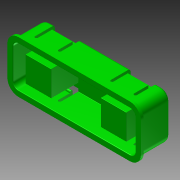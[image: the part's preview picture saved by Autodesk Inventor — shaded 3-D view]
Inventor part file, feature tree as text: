
AUTODESK INVENTOR PART (.ipt)
format: ipt  version: 2015 (Build 190159000, 159)  size: 282,624 bytes
history: native  units: in
note: dims shown in document units (in); Inventor stores cm internally (conversion verified against a paired STEP export)
features: fillet x6, extrude x4, sketch x3, shell x2, plane x2, mirror x2
ambient origin geometry x8: Origin, YZ Plane, XZ Plane, XY Plane, X Axis, Y Axis, Z Axis, Center Point
bodies: Solid1 (feature_tree)
feature tree (19):
  extrude  "Extrusion1"  Depth=0.465in
  fillet  "Fillet1"  Radius=0.57in
  shell  "Shell1"  Thickness=0.2in
  sketch  "Sketch2"  dims[d7=0.46in d8=0.2283in]
  plane  "Work Plane1"
  sketch  "Sketch3"  dims[d9=-0.033in d10=0.47in d11=0.0in d12=0.005in d13=0.01in d14=0.47in d15=0.05in d16=0.1in d17=0.05in d18=0.05in d19=0.15in d20=0.0in d21=0.125in d22=0.0in d23=0.05in d24=0.03in d26=0.445in d27=0.445in d28=0.05in]
  shell  "Shell2"  Thickness=0.1in
  extrude  "Extrusion3"  Depth=0.46in
  plane  "Work Plane2"
  extrude  "Extrusion4"  Depth=0.47in TaperAngle=0.0deg
  fillet  "Fillet6"  Radius=0.005in
  fillet  "Fillet3"  Radius=0.01in
  fillet  "Fillet4"  Radius=0.47in
  extrude  "Extrusion2"  Depth=0.05in
  fillet  "Fillet2"  Radius=0.1in
  fillet  "Fillet7"  Radius=0.05in
  mirror  "Mirror1"
  mirror  "Mirror2"
  sketch  "Sketch1"  dims[d0=1.2in d1=0.465in d2=0.57in d3=0.0in d4=0.2in d5=0.1in]
